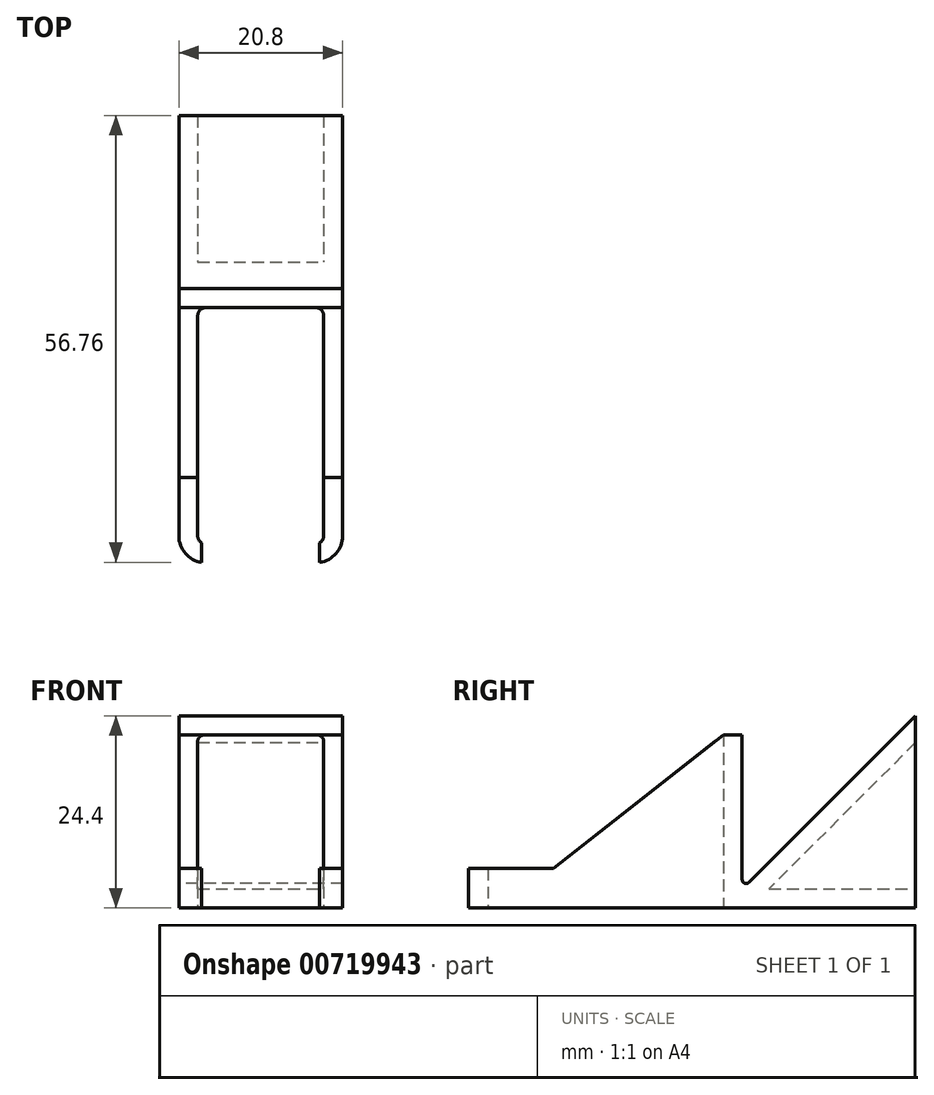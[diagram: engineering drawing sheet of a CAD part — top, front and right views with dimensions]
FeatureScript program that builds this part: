
annotation { "Feature Type Name" : "Feature", "Feature Type Description" : "" }
export const myFeature = defineFeature(function(context is Context, id is Id, definition is map)
    precondition{}
    {
        {
            assignVariable(context, id + "F0", {"name" : "holder_x_size", "anyValue" : 16});
        }
        {
            assignVariable(context, id + "F1", {"name" : "holder_height", "anyValue" : 5});
        }
        {
            assignVariable(context, id + "F2", {"name" : "wall_thickness", "anyValue" : 6 * 0.4});
        }
        {
            assignVariable(context, id + "F3", {"name" : "backplate_width", "anyValue" : max(15, getVariable(context, 'holder_x_size') + 2 * getVariable(context, 'wall_thickness'))});
        }
        {
            assignVariable(context, id + "F4", {"name" : "backplate_height", "anyValue" : max(22, getVariable(context, 'holder_height'))});
        }
        {
            var Q0;
            Q0=qCreatedBy(makeId("Right.planeOp"),FACE);
            var sketch = newSketch(context, id + "F5", { "sketchPlane" : qUnion([Q0])});
            skLineSegment(sketch, "E0", {"start": v(24.4, 24.4) * mm, "end": v(24.4, 0) * mm});
            skLineSegment(sketch, "E1", {"start": v(24.4, 24.4) * mm, "end": v(3.25, 3.25) * mm});
            skLineSegment(sketch, "E2", {"start": v(2.4, 22) * mm, "end": v(2.4, 3.6) * mm});
            skLineSegment(sketch, "E3", {"start": v(0, 0) * mm, "end": v(0, 22) * mm});
            skLineSegment(sketch, "E4", {"start": v(0, 0) * mm, "end": v(24.4, 0) * mm});
            skLineSegment(sketch, "E5", {"start": v(0, 22) * mm, "end": v(2.4, 22) * mm});
            skPoint(sketch, "E6.visualSharp", {"position": v(2.4, 2.4) * mm});
            skArc(sketch, "E6.filletArc", {"start": v(2.4, 3.6) * mm, "mid": v(2.7, 3.15) * mm, "end": v(3.25, 3.25) * mm});
            skPoint(sketch, "E7.visualSharp", {"position": v(2.4, 0) * mm});
            skSolve(sketch);
        }
        {
            var Q0;
            Q0 = qSketchRegion(id + "F5", true);
            extrude(context, id + "F6", {"entities" : qUnion([Q0]), "endBound" : BoundingType.SYMMETRIC, "depth" : (getVariable(context, 'backplate_width')) * mm, "offsetDistance" : 25 * mm});
        }
        {
            var Q0;
            Q0=qCreatedBy(makeId("Top.planeOp"),FACE);
            var sketch = newSketch(context, id + "F7", { "sketchPlane" : qUnion([Q0])});
            skLineSegment(sketch, "E8.bottom", {"start": v(-10.4, 0) * mm, "end": v(10.4, 0) * mm});
            skLineSegment(sketch, "E8.top", {"start": v(-7, -30) * mm, "end": v(7, -30) * mm});
            skLineSegment(sketch, "E8.left", {"start": v(-8, -1) * mm, "end": v(-8, -29) * mm});
            skLineSegment(sketch, "E8.right", {"start": v(8, -1) * mm, "end": v(8, -29) * mm});
            skPoint(sketch, "E9.visualSharp", {"position": v(-8, 0) * mm});
            skArc(sketch, "E9.filletArc", {"start": v(-7, 0) * mm, "mid": v(-7.7, -0.3) * mm, "end": v(-8, -1) * mm});
            skPoint(sketch, "E10.visualSharp", {"position": v(8, 0) * mm});
            skArc(sketch, "E10.filletArc", {"start": v(8, -1) * mm, "mid": v(7.7, -0.3) * mm, "end": v(7, 0) * mm});
            skPoint(sketch, "E11.visualSharp", {"position": v(8, -30) * mm});
            skArc(sketch, "E11.filletArc", {"start": v(7, -30) * mm, "mid": v(7.7, -29.7) * mm, "end": v(8, -29) * mm});
            skPoint(sketch, "E12.visualSharp", {"position": v(-8, -30) * mm});
            skArc(sketch, "E12.filletArc", {"start": v(-8, -29) * mm, "mid": v(-7.7, -29.7) * mm, "end": v(-7, -30) * mm});
            skLineSegment(sketch, "E13.2", {"start": v(-10.4, -21.6) * mm, "end": v(-10.4, -29) * mm});
            skLineSegment(sketch, "E13.4", {"start": v(10.4, -21.6) * mm, "end": v(10.4, -29) * mm});
            skArc(sketch, "E13.7", {"start": v(-10.4, -29) * mm, "mid": v(-9.4, -31.4) * mm, "end": v(-7, -32.4) * mm});
            skArc(sketch, "E13.9", {"start": v(7, -32.4) * mm, "mid": v(9.4, -31.4) * mm, "end": v(10.4, -29) * mm});
            skLineSegment(sketch, "E14", {"start": v(-10.4, 4.93) * mm, "end": v(10.4, 4.93) * mm, "construction": true});
            skLineSegment(sketch, "E15", {"start": v(10.4, 4.93) * mm, "end": v(10.4, 14.95) * mm, "construction": true});
            skPoint(sketch, "E16.orphan", {"position": v(10.4, 0) * mm});
            skLineSegment(sketch, "E17", {"start": v(-12.75, 0) * mm, "end": v(-12.75, -10.8) * mm, "construction": true});
            skLineSegment(sketch, "E18", {"start": v(-12.75, -10.8) * mm, "end": v(-12.75, -21.6) * mm, "construction": true});
            skLineSegment(sketch, "E19", {"start": v(-12.75, -21.6) * mm, "end": v(-12.75, -32.4) * mm, "construction": true});
            skLineSegment(sketch, "E20", {"start": v(-12.75, -21.6) * mm, "end": v(16.88, -21.6) * mm, "construction": true});
            skLineSegment(sketch, "E21", {"start": v(-10.4, -21.6) * mm, "end": v(-10.4, 0) * mm});
            skLineSegment(sketch, "E22", {"start": v(10.4, 0) * mm, "end": v(10.4, -21.6) * mm});
            skLineSegment(sketch, "E23.trimOffspring", {"start": v(-7, -32.4) * mm, "end": v(7, -32.4) * mm});
            skSolve(sketch);
        }
        {
            var Q0;
            Q0=makeQuery(id+"F7.imprint","IMPRINT",FACE,{"disambiguationData":[TD([[makeQuery(id+"F7.imprint","IMPRINT",EDGE,{"derivedFrom":sQuery(id+"F7.wireOp",EDGE,"E8.top")}),-1.0]])]});
            extrude(context, id + "F8", {"entities" : qUnion([Q0]), "operationType" : NewBodyOperationType.ADD, "depth" : (getVariable(context, 'backplate_height')) * mm, "offsetDistance" : 25 * mm});
        }
        {
            var Q0;
            Q0=qCreatedBy(makeId("Top.planeOp"),FACE);
            var sketch = newSketch(context, id + "F9", { "sketchPlane" : qUnion([Q0])});
            skLineSegment(sketch, "E24.bottom", {"start": v(7.5, -29) * mm, "end": v(-7.5, -29) * mm});
            skLineSegment(sketch, "E24.top", {"start": v(7.5, -32.4) * mm, "end": v(-7.5, -32.4) * mm});
            skLineSegment(sketch, "E24.left", {"start": v(7.5, -29) * mm, "end": v(7.5, -32.4) * mm});
            skLineSegment(sketch, "E24.right", {"start": v(-7.5, -29) * mm, "end": v(-7.5, -32.4) * mm});
            skSolve(sketch);
        }
        {
            var Q0;
            Q0=makeQuery(id+"F9.imprint","IMPRINT",FACE,{"disambiguationData":[TD([[makeQuery(id+"F9.imprint","IMPRINT",EDGE,{"derivedFrom":sQuery(id+"F9.wireOp",EDGE,"E24.bottom")}),1.0]])]});
            extrude(context, id + "F10", {"entities" : qUnion([Q0]), "operationType" : NewBodyOperationType.REMOVE, "endBound" : BoundingType.THROUGH_ALL, "depth" : 25 * mm, "offsetDistance" : 25 * mm});
        }
        {
            var Q0;
            Q0=qCreatedBy(makeId("Right.planeOp"),FACE);
            var sketch = newSketch(context, id + "F11", { "sketchPlane" : qUnion([Q0])});
            skLineSegment(sketch, "E25", {"start": v(-32.4, 5) * mm, "end": v(-32.4, 22) * mm});
            skLineSegment(sketch, "E26", {"start": v(-32.4, 22) * mm, "end": v(0, 22) * mm});
            skLineSegment(sketch, "E27", {"start": v(0, 23.92) * mm, "end": v(-10.8, 23.92) * mm, "construction": true});
            skLineSegment(sketch, "E28", {"start": v(-10.8, 23.92) * mm, "end": v(-21.6, 23.92) * mm, "construction": true});
            skLineSegment(sketch, "E29", {"start": v(-21.6, 23.92) * mm, "end": v(-32.4, 23.92) * mm, "construction": true});
            skLineSegment(sketch, "E30", {"start": v(-21.6, 23.92) * mm, "end": v(-21.6, 5) * mm, "construction": true});
            skLineSegment(sketch, "E31", {"start": v(0, 22) * mm, "end": v(-21.6, 5) * mm});
            skLineSegment(sketch, "E32", {"start": v(-32.4, 5) * mm, "end": v(-21.6, 5) * mm});
            skSolve(sketch);
        }
        {
            var Q0;
            Q0=makeQuery(id+"F11.imprint","IMPRINT",FACE,{"disambiguationData":[TD([[makeQuery(id+"F11.imprint","IMPRINT",EDGE,{"derivedFrom":sQuery(id+"F11.wireOp",EDGE,"E25")}),-1.0]])]});
            extrude(context, id + "F12", {"entities" : qUnion([Q0]), "operationType" : NewBodyOperationType.REMOVE, "endBound" : BoundingType.THROUGH_ALL, "depth" : 25 * mm, "offsetDistance" : 25 * mm, "hasSecondDirection" : true, "secondDirectionBound" : SecondDirectionBoundingType.THROUGH_ALL, "secondDirectionOppositeDirection" : true, "secondDirectionDepth" : 25 * mm});
        }
        {
            var Q0;
            Q0=qCreatedBy(makeId("Right.planeOp"),FACE);
            var sketch = newSketch(context, id + "F13", { "sketchPlane" : qUnion([Q0])});
            skLineSegment(sketch, "E33.bottom", {"start": v(0, 22) * mm, "end": v(2.4, 22) * mm});
            skLineSegment(sketch, "E33.top", {"start": v(0, 2.4) * mm, "end": v(2.4, 2.4) * mm, "construction": true});
            skLineSegment(sketch, "E33.left", {"start": v(2.4, 22) * mm, "end": v(2.4, 2.4) * mm});
            skLineSegment(sketch, "E33.right", {"start": v(0, 22) * mm, "end": v(0, 2.4) * mm});
            skLineSegment(sketch, "E34", {"start": v(24.4, 21) * mm, "end": v(5.8, 2.4) * mm});
            skLineSegment(sketch, "E35", {"start": v(5.8, 2.4) * mm, "end": v(24.4, 2.4) * mm});
            skLineSegment(sketch, "E36", {"start": v(24.4, 2.4) * mm, "end": v(24.4, 21) * mm});
            skSolve(sketch);
        }
        {
            var Q0;
            Q0 = qSketchRegion(id + "F13", true);
            extrude(context, id + "F14", {"entities" : qUnion([Q0]), "operationType" : NewBodyOperationType.REMOVE, "endBound" : BoundingType.SYMMETRIC, "oppositeDirection" : true, "depth" : (getVariable(context, 'backplate_width') - 2 * getVariable(context, 'wall_thickness')) * mm, "offsetDistance" : 25 * mm});
        }
    });
